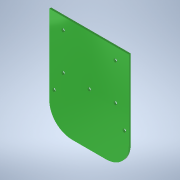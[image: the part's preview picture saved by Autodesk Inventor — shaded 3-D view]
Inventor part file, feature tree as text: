
AUTODESK INVENTOR PART (.ipt)
format: ipt  version: 2022 (Build 260153000, 153)  size: 152,576 bytes
history: native  units: mm
features: sketch x3, other x2, extrude x2, fillet x1, hole x1
ambient origin geometry x8: Origin, YZ Plane, XZ Plane, XY Plane, X Axis, Y Axis, Z Axis, Center Point
bodies: Body1 (feature_tree)
feature tree (9):
  other  "FS90-Mount2.ipt"
  other  "ソリッド1"
  extrude  "押し出し1"  Depth=70.0mm
  fillet  "フィレット1"  Radius=90.0mm
  hole  "穴1"  [1 undecoded]
  extrude  "押し出し2"  Depth=20.0mm
  sketch  "スケッチ1"
  sketch  "スケッチ2"
  sketch  "スケッチ3"
note: 1 required parameter value undecoded (feature->parameter linkage not recoverable at this tier; creation-order binding heuristic only, values carry confidence <= 0.55)
